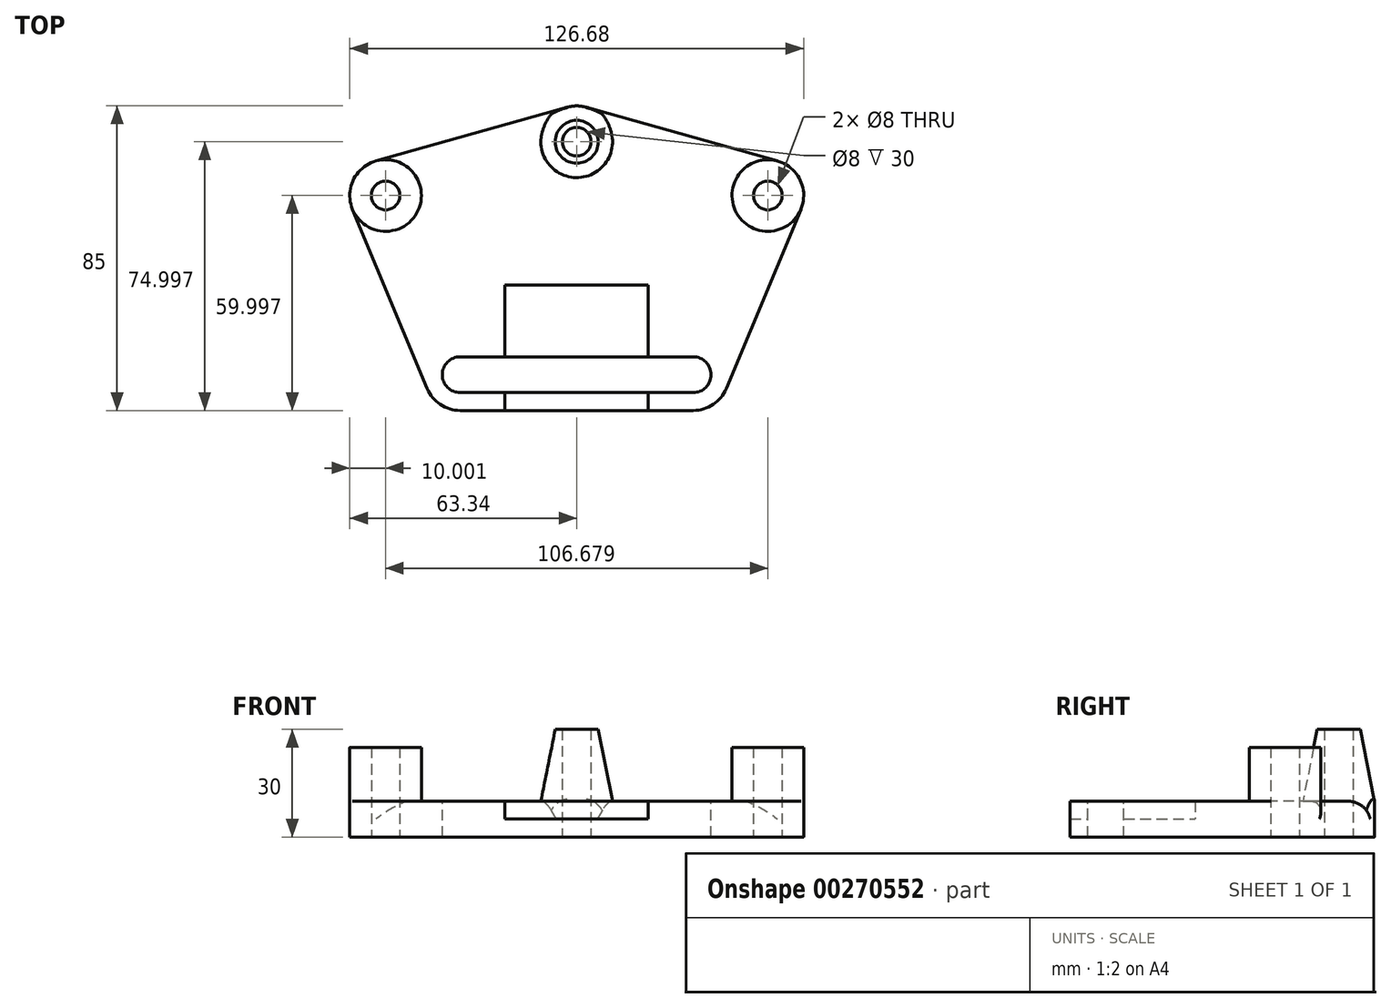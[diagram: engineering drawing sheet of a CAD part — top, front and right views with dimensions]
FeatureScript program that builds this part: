
annotation { "Feature Type Name" : "Feature", "Feature Type Description" : "" }
export const myFeature = defineFeature(function(context is Context, id is Id, definition is map)
    precondition{}
    {
        {
            var Q0;
            Q0=qCreatedBy(makeId("Top.planeOp"),FACE);
            var sketch = newSketch(context, id + "F0", { "sketchPlane" : qUnion([Q0])});
            skLineSegment(sketch, "E0", {"start": v(2.7, 41.21) * mm, "end": v(56.05, 26.21) * mm});
            skLineSegment(sketch, "E1", {"start": v(62.57, 12.74) * mm, "end": v(41.73, -37.26) * mm});
            skLineSegment(sketch, "E2", {"start": v(32.5, -43.41) * mm, "end": v(-32.5, -43.41) * mm});
            skLineSegment(sketch, "E3", {"start": v(-41.73, -37.26) * mm, "end": v(-62.57, 12.74) * mm});
            skLineSegment(sketch, "E4", {"start": v(-56.05, 26.21) * mm, "end": v(-2.7, 41.21) * mm});
            skPoint(sketch, "E5.visualSharp", {"position": v(0, 41.98) * mm});
            skArc(sketch, "E5.filletArc", {"start": v(2.7, 41.21) * mm, "mid": v(0, 41.59) * mm, "end": v(-2.7, 41.21) * mm});
            skPoint(sketch, "E6.visualSharp", {"position": v(-66.91, 23.16) * mm});
            skArc(sketch, "E6.filletArc", {"start": v(-56.05, 26.21) * mm, "mid": v(-62.34, 20.94) * mm, "end": v(-62.57, 12.74) * mm});
            skPoint(sketch, "E7.visualSharp", {"position": v(66.91, 23.16) * mm});
            skArc(sketch, "E7.filletArc", {"start": v(62.57, 12.74) * mm, "mid": v(62.34, 20.94) * mm, "end": v(56.05, 26.21) * mm});
            skPoint(sketch, "E8.visualSharp", {"position": v(39.17, -43.41) * mm});
            skArc(sketch, "E8.filletArc", {"start": v(32.5, -43.41) * mm, "mid": v(38.05, -41.73) * mm, "end": v(41.73, -37.26) * mm});
            skPoint(sketch, "E9.visualSharp", {"position": v(-39.17, -43.41) * mm});
            skArc(sketch, "E9.filletArc", {"start": v(-41.73, -37.26) * mm, "mid": v(-38.05, -41.73) * mm, "end": v(-32.5, -43.41) * mm});
            skSolve(sketch);
        }
        {
            var Q0;
            Q0=makeQuery(id+"F0.imprint","IMPRINT",FACE,{"disambiguationData":[TD([[makeQuery(id+"F0.imprint","IMPRINT",EDGE,{"derivedFrom":sQuery(id+"F0.wireOp",EDGE,"E0")}),-1.0]])]});
            extrude(context, id + "F1", {"entities" : qUnion([Q0]), "depth" : 10 * mm});
        }
        {
            var Q0;
            Q0=makeQuery(id+"F1.opExtrude","CAP_FACE",FACE,{"disambiguationData":[OSD([sQuery(id+"F0.wireOp",EDGE,"E0"),sQuery(id+"F0.wireOp",EDGE,"E1"),sQuery(id+"F0.wireOp",EDGE,"E2"),sQuery(id+"F0.wireOp",EDGE,"E3"),sQuery(id+"F0.wireOp",EDGE,"E4"),sQuery(id+"F0.wireOp",EDGE,"E5.filletArc"),sQuery(id+"F0.wireOp",EDGE,"E6.filletArc"),sQuery(id+"F0.wireOp",EDGE,"E7.filletArc"),sQuery(id+"F0.wireOp",EDGE,"E8.filletArc"),sQuery(id+"F0.wireOp",EDGE,"E9.filletArc")])],"isStart":false});
            var sketch = newSketch(context, id + "F2", { "sketchPlane" : qUnion([Q0])});
            skCircle(sketch, "E10", {"center": v(-53.34, 16.59) * mm, "radius": 10 * mm});
            skCircle(sketch, "E11", {"center": v(53.34, 16.59) * mm, "radius": 10 * mm});
            skSolve(sketch);
        }
        {
            var Q0;
            {var subQ0=sQuery(id+"F2.wireOp",EDGE,"E10");var subQ1=makeQuery(id+"F2.imprint","INTERSECT",VERTEX,{"derivedFrom":[makeQuery(id+"F1.opExtrude","CAP_EDGE",EDGE,{"disambiguationData":[OSD([sQuery(id+"F0.wireOp",EDGE,"E3")])],"isStart":false}),subQ0]});Q0=makeQuery(id+"F2.imprint","IMPRINT",FACE,{"disambiguationData":[TD([[makeQuery(id+"F2.imprint","IMPRINT",EDGE,{"disambiguationData":[TD([[subQ1,1.0]])],"derivedFrom":subQ0}),1.0]])]});}
            var Q1;
            {var subQ0=sQuery(id+"F2.wireOp",EDGE,"E11");var subQ1=makeQuery(id+"F2.imprint","INTERSECT",VERTEX,{"derivedFrom":[makeQuery(id+"F1.opExtrude","CAP_EDGE",EDGE,{"disambiguationData":[OSD([sQuery(id+"F0.wireOp",EDGE,"E0")])],"isStart":false}),subQ0]});Q1=makeQuery(id+"F2.imprint","IMPRINT",FACE,{"disambiguationData":[TD([[makeQuery(id+"F2.imprint","IMPRINT",EDGE,{"disambiguationData":[TD([[subQ1,1.0]])],"derivedFrom":subQ0}),1.0]])]});}
            extrude(context, id + "F3", {"entities" : qUnion([Q0, Q1]), "operationType" : NewBodyOperationType.ADD, "depth" : 15 * mm});
        }
        {
            var Q0;
            Q0=qCreatedBy(makeId("Right.planeOp"),FACE);
            var sketch = newSketch(context, id + "F4", { "sketchPlane" : qUnion([Q0])});
            skLineSegment(sketch, "E12", {"start": v(21.59, 10) * mm, "end": v(31.59, 10) * mm});
            skLineSegment(sketch, "E13", {"start": v(31.59, 10) * mm, "end": v(31.59, 30) * mm});
            skLineSegment(sketch, "E14", {"start": v(31.59, 30) * mm, "end": v(25.59, 30) * mm});
            skLineSegment(sketch, "E15", {"start": v(25.59, 30) * mm, "end": v(21.59, 10) * mm});
            skSolve(sketch);
        }
        {
            var Q0;
            Q0=makeQuery(id+"F4.imprint","IMPRINT",FACE,{"disambiguationData":[TD([[makeQuery(id+"F4.imprint","IMPRINT",EDGE,{"derivedFrom":sQuery(id+"F4.wireOp",EDGE,"E12")}),1.0]])]});
            var Q1;
            Q1=sQuery(id+"F4.wireOp",EDGE,"E13");
            revolve(context, id + "F5", {"operationType" : NewBodyOperationType.ADD, "entities" : qUnion([Q0]), "axis" : qUnion([Q1]), "revolveType" : RevolveType.FULL});
        }
        {
            var Q0;
            Q0=makeQuery(id+"F1.opExtrude","CAP_FACE",FACE,{"disambiguationData":[OSD([sQuery(id+"F0.wireOp",EDGE,"E0"),sQuery(id+"F0.wireOp",EDGE,"E1"),sQuery(id+"F0.wireOp",EDGE,"E2"),sQuery(id+"F0.wireOp",EDGE,"E3"),sQuery(id+"F0.wireOp",EDGE,"E4"),sQuery(id+"F0.wireOp",EDGE,"E5.filletArc"),sQuery(id+"F0.wireOp",EDGE,"E6.filletArc"),sQuery(id+"F0.wireOp",EDGE,"E7.filletArc"),sQuery(id+"F0.wireOp",EDGE,"E8.filletArc"),sQuery(id+"F0.wireOp",EDGE,"E9.filletArc")])],"isStart":false});
            var sketch = newSketch(context, id + "F6", { "sketchPlane" : qUnion([Q0])});
            skCircle(sketch, "E16", {"center": v(-53.34, 16.59) * mm, "radius": 4 * mm});
            skCircle(sketch, "E17", {"center": v(0, 31.59) * mm, "radius": 4 * mm});
            skCircle(sketch, "E18", {"center": v(53.34, 16.59) * mm, "radius": 4 * mm});
            skArc(sketch, "E19", {"start": v(32.5, -38.41) * mm, "mid": v(37.5, -33.41) * mm, "end": v(32.5, -28.41) * mm});
            skArc(sketch, "E20", {"start": v(-32.5, -28.41) * mm, "mid": v(-37.5, -33.41) * mm, "end": v(-32.5, -38.41) * mm});
            skLineSegment(sketch, "E21", {"start": v(-32.5, -28.41) * mm, "end": v(32.5, -28.41) * mm});
            skLineSegment(sketch, "E22", {"start": v(-32.5, -38.41) * mm, "end": v(32.5, -38.41) * mm});
            skSolve(sketch);
        }
        {
            var Q0;
            Q0 = qSketchRegion(id + "F6", true);
            extrude(context, id + "F7", {"entities" : qUnion([Q0]), "operationType" : NewBodyOperationType.REMOVE, "endBound" : BoundingType.THROUGH_ALL, "depth" : 50 * mm});
        }
        {
            var Q0;
            Q0 = qSketchRegion(id + "F6", true);
            extrude(context, id + "F8", {"entities" : qUnion([Q0]), "operationType" : NewBodyOperationType.REMOVE, "endBound" : BoundingType.THROUGH_ALL, "oppositeDirection" : true, "depth" : 25 * mm});
        }
        {
            var Q0;
            Q0=makeQuery(id+"F3.opExtrude","CAP_EDGE",EDGE,{"disambiguationData":[OSD([sQuery(id+"F2.wireOp",EDGE,"E10")])],"isStart":true});
            var Q1;
            Q1=makeQuery(id+"F5.opRevolve","SWEPT_EDGE",EDGE,{"disambiguationData":[OSD([sQuery(id+"F4.wireOp",EDGE,"E12"),sQuery(id+"F4.wireOp",EDGE,"E15")])]});
            var Q2;
            Q2=makeQuery(id+"F3.opExtrude","CAP_EDGE",EDGE,{"disambiguationData":[OSD([sQuery(id+"F2.wireOp",EDGE,"E11")])],"isStart":true});
            fillet(context, id + "F9", {"entities" : qUnion([Q0, Q1, Q2]), "radius" : 5 * mm, "tangentPropagation" : true, "allowEdgeOverflow" : false});
        }
        {
            var Q0;
            Q0=qCreatedBy(makeId("Right.planeOp"),FACE);
            var sketch = newSketch(context, id + "F10", { "sketchPlane" : qUnion([Q0])});
            skLineSegment(sketch, "E23.bottom", {"start": v(-43.41, 10) * mm, "end": v(-8.41, 10) * mm});
            skLineSegment(sketch, "E23.top", {"start": v(-43.41, 5) * mm, "end": v(-8.41, 5) * mm});
            skLineSegment(sketch, "E23.left", {"start": v(-43.41, 10) * mm, "end": v(-43.41, 5) * mm});
            skLineSegment(sketch, "E23.right", {"start": v(-8.41, 10) * mm, "end": v(-8.41, 5) * mm});
            skSolve(sketch);
        }
        {
            var Q0;
            Q0=makeQuery(id+"F10.imprint","IMPRINT",FACE,{"disambiguationData":[TD([[makeQuery(id+"F10.imprint","IMPRINT",EDGE,{"derivedFrom":sQuery(id+"F10.wireOp",EDGE,"E23.bottom")}),-1.0]])]});
            extrude(context, id + "F11", {"entities" : qUnion([Q0]), "operationType" : NewBodyOperationType.REMOVE, "endBound" : BoundingType.SYMMETRIC, "oppositeDirection" : true, "depth" : 40 * mm});
        }
    });
